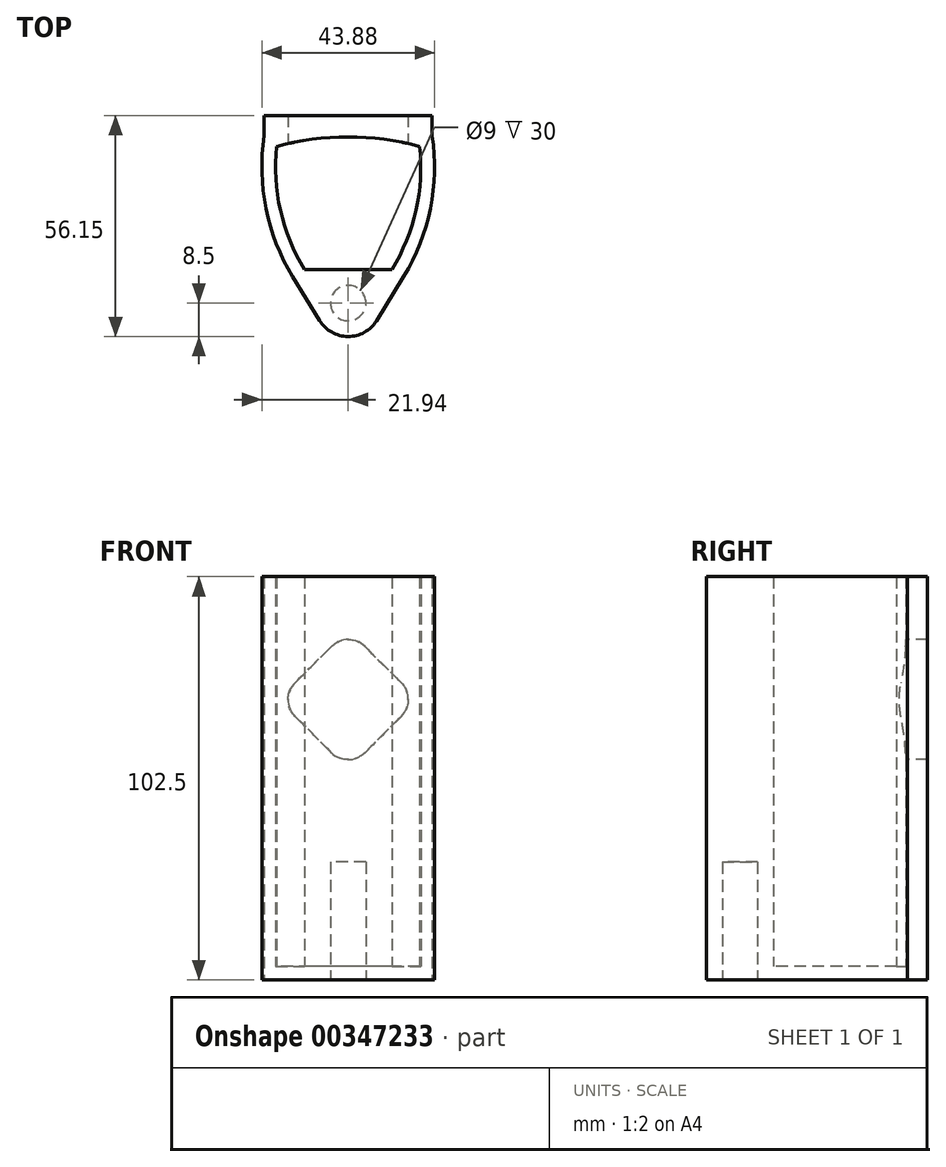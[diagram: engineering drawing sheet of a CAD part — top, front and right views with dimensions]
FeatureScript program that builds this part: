
annotation { "Feature Type Name" : "Feature", "Feature Type Description" : "" }
export const myFeature = defineFeature(function(context is Context, id is Id, definition is map)
    precondition{}
    {
        {
            var Q0;
            Q0=qCreatedBy(makeId("Top.planeOp"),FACE);
            var sketch = newSketch(context, id + "F0", { "sketchPlane" : qUnion([Q0])});
            skLineSegment(sketch, "E0", {"start": v(0, 0) * mm, "end": v(11.12, 0) * mm});
            skLineSegment(sketch, "E1", {"start": v(11.12, 0) * mm, "end": v(-11.12, 0) * mm});
            skArc(sketch, "E2", {"start": v(-18.16, 31.28) * mm, "mid": v(-17.22, 15.06) * mm, "end": v(-11.13, 0) * mm});
            skArc(sketch, "E3", {"start": v(11.13, 0) * mm, "mid": v(17.22, 15.06) * mm, "end": v(18.16, 31.28) * mm});
            skArc(sketch, "E4", {"start": v(18.16, 31.28) * mm, "mid": v(0, 33.7) * mm, "end": v(-18.16, 31.28) * mm});
            skArc(sketch, "E5.0", {"start": v(-21.34, 34) * mm, "mid": v(-20.88, 15.46) * mm, "end": v(-14.11, -1.82) * mm});
            skArc(sketch, "E5.1", {"start": v(21.34, 34) * mm, "mid": v(0, 37.2) * mm, "end": v(-21.34, 34) * mm});
            skArc(sketch, "E5.2", {"start": v(14.11, -1.82) * mm, "mid": v(20.88, 15.46) * mm, "end": v(21.34, 34) * mm});
            skCircle(sketch, "E6", {"center": v(0, -8.5) * mm, "radius": 4.5 * mm});
            skLineSegment(sketch, "E7", {"start": v(-14.11, -1.82) * mm, "end": v(-7.23, -12.97) * mm});
            skLineSegment(sketch, "E8", {"start": v(7.19, -13.03) * mm, "end": v(14.11, -1.82) * mm});
            skArc(sketch, "E9", {"start": v(-7.23, -12.97) * mm, "mid": v(-0.04, -17) * mm, "end": v(7.19, -13.03) * mm});
            skLineSegment(sketch, "E10", {"start": v(21.34, 34) * mm, "end": v(21.34, 39.15) * mm});
            skLineSegment(sketch, "E11", {"start": v(21.34, 39.15) * mm, "end": v(-21.34, 39.15) * mm});
            skLineSegment(sketch, "E12", {"start": v(-21.34, 39.15) * mm, "end": v(-21.34, 34) * mm});
            skSolve(sketch);
        }
        {
            var Q0;
            {var subQ3=sQuery(id+"F0.wireOp",EDGE,"E2");Q0=makeQuery(id+"F0.imprint","IMPRINT",FACE,{"disambiguationData":[TD([[makeQuery(id+"F0.imprint","IMPRINT",EDGE,{"derivedFrom":subQ3}),-1.0]])]});}
            var Q1;
            Q1=makeQuery(id+"F0.imprint","IMPRINT",FACE,{"disambiguationData":[TD([[makeQuery(id+"F0.imprint","IMPRINT",EDGE,{"derivedFrom":sQuery(id+"F0.wireOp",EDGE,"E6")}),1.0]])]});
            extrude(context, id + "F1", {"entities" : qUnion([Q0, Q1]), "depth" : 102.5 * mm});
        }
        {
            var Q0;
            {var subQ1=sQuery(id+"F0.wireOp",EDGE,"E2");Q0=makeQuery(id+"F0.imprint","IMPRINT",FACE,{"disambiguationData":[TD([[makeQuery(id+"F0.imprint","IMPRINT",EDGE,{"derivedFrom":subQ1}),1.0]])]});}
            extrude(context, id + "F2", {"entities" : qUnion([Q0]), "operationType" : NewBodyOperationType.ADD, "depth" : 3.5 * mm});
        }
        {
            var Q0;
            Q0=makeQuery(id+"F0.imprint","IMPRINT",FACE,{"disambiguationData":[TD([[makeQuery(id+"F0.imprint","IMPRINT",EDGE,{"derivedFrom":sQuery(id+"F0.wireOp",EDGE,"E6")}),1.0]])]});
            extrude(context, id + "F3", {"entities" : qUnion([Q0]), "operationType" : NewBodyOperationType.REMOVE, "depth" : 30 * mm});
        }
        {
            var Q0;
            Q0=makeQuery(id+"F0.imprint","IMPRINT",FACE,{"disambiguationData":[TD([[makeQuery(id+"F0.imprint","IMPRINT",EDGE,{"derivedFrom":sQuery(id+"F0.wireOp",EDGE,"E5.1")}),-1.0]])]});
            extrude(context, id + "F4", {"entities" : qUnion([Q0]), "operationType" : NewBodyOperationType.ADD, "depth" : 102.5 * mm});
        }
        {
            var Q0;
            Q0=makeQuery(id+"F4.opExtrude","SWEPT_FACE",FACE,{"disambiguationData":[OSD([sQuery(id+"F0.wireOp",EDGE,"E11")])]});
            var sketch = newSketch(context, id + "F5", { "sketchPlane" : qUnion([Q0])});
            skPoint(sketch, "E13.endSnap0", {"position": v(0, 0) * mm});
            skLineSegment(sketch, "E14", {"start": v(-17.75, 71.25) * mm, "end": v(0, 89) * mm});
            skLineSegment(sketch, "E15", {"start": v(17.75, 71.25) * mm, "end": v(0, 53.5) * mm});
            skLineSegment(sketch, "E16", {"start": v(0, 53.5) * mm, "end": v(-17.75, 71.25) * mm});
            skLineSegment(sketch, "E17", {"start": v(0, 89) * mm, "end": v(17.75, 71.25) * mm});
            skSolve(sketch);
        }
        {
            var Q0;
            Q0=makeQuery(id+"F5.imprint","IMPRINT",FACE,{"disambiguationData":[TD([[makeQuery(id+"F5.imprint","IMPRINT",EDGE,{"derivedFrom":sQuery(id+"F5.wireOp",EDGE,"E14")}),-1.0]])]});
            extrude(context, id + "F6", {"entities" : qUnion([Q0]), "operationType" : NewBodyOperationType.REMOVE, "oppositeDirection" : true, "depth" : 10 * mm});
        }
        {
            var Q0;
            Q0=makeQuery(id+"F6.boolean.opBoolean","COPY",EDGE,{"derivedFrom":makeQuery(id+"F6.opExtrude","SWEPT_EDGE",EDGE,{"disambiguationData":[OSD([sQuery(id+"F5.wireOp",EDGE,"E15"),sQuery(id+"F5.wireOp",EDGE,"E17")])]})});
            var Q1;
            Q1=makeQuery(id+"F6.boolean.opBoolean","COPY",EDGE,{"derivedFrom":makeQuery(id+"F6.opExtrude","SWEPT_EDGE",EDGE,{"disambiguationData":[OSD([sQuery(id+"F5.wireOp",EDGE,"E15"),sQuery(id+"F5.wireOp",EDGE,"E16")])]})});
            var Q2;
            Q2=makeQuery(id+"F6.boolean.opBoolean","COPY",EDGE,{"derivedFrom":makeQuery(id+"F6.opExtrude","SWEPT_EDGE",EDGE,{"disambiguationData":[OSD([sQuery(id+"F5.wireOp",EDGE,"E14"),sQuery(id+"F5.wireOp",EDGE,"E16")])]})});
            var Q3;
            Q3=makeQuery(id+"F6.boolean.opBoolean","COPY",EDGE,{"derivedFrom":makeQuery(id+"F6.opExtrude","SWEPT_EDGE",EDGE,{"disambiguationData":[OSD([sQuery(id+"F5.wireOp",EDGE,"E14"),sQuery(id+"F5.wireOp",EDGE,"E17")])]})});
            fillet(context, id + "F7", {"entities" : qUnion([Q0, Q1, Q2, Q3]), "radius" : 6 * mm, "tangentPropagation" : true, "allowEdgeOverflow" : false});
        }
    });
